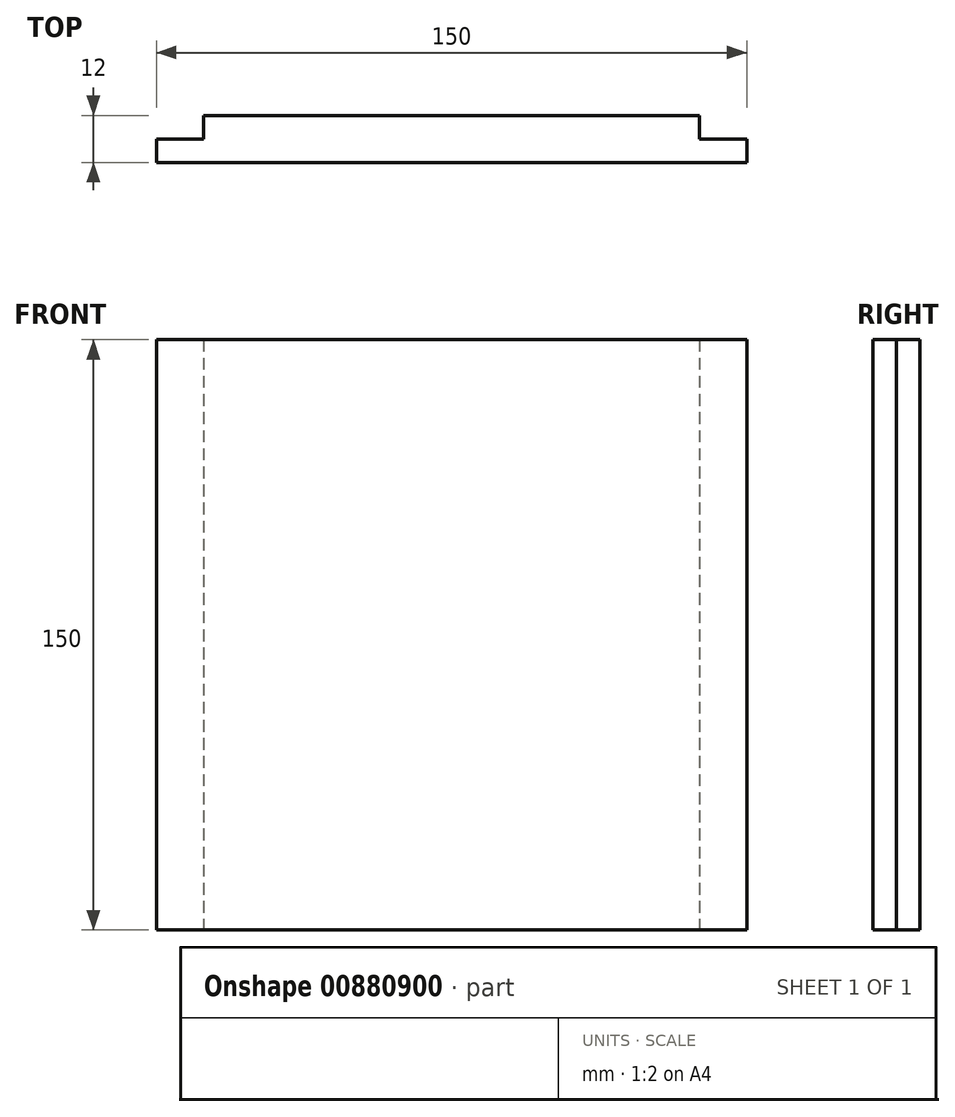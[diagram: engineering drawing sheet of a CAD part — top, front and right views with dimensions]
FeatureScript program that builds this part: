
annotation { "Feature Type Name" : "Feature", "Feature Type Description" : "" }
export const myFeature = defineFeature(function(context is Context, id is Id, definition is map)
    precondition{}
    {
        {
            var Q0;
            Q0=qCreatedBy(makeId("Top.planeOp"),FACE);
            var sketch = newSketch(context, id + "F0", { "sketchPlane" : qUnion([Q0])});
            skLineSegment(sketch, "E0.bottom", {"start": v(63, 6) * mm, "end": v(-63, 6) * mm});
            skLineSegment(sketch, "E0.top", {"start": v(75, -6) * mm, "end": v(-75, -6) * mm});
            skLineSegment(sketch, "E0.left", {"start": v(75, 0) * mm, "end": v(75, -6) * mm});
            skLineSegment(sketch, "E0.right", {"start": v(-75, 0) * mm, "end": v(-75, -6) * mm});
            skPoint(sketch, "E0.middle", {"position": v(0, 0) * mm});
            skLineSegment(sketch, "E1", {"start": v(-75, 0) * mm, "end": v(-63, 0) * mm});
            skLineSegment(sketch, "E2", {"start": v(-63, 0) * mm, "end": v(-63, 6) * mm});
            skLineSegment(sketch, "E3", {"start": v(75, 0) * mm, "end": v(63, 0) * mm});
            skLineSegment(sketch, "E4", {"start": v(63, 0) * mm, "end": v(63, 6) * mm});
            skPoint(sketch, "E5.orphan", {"position": v(75, 6) * mm});
            skPoint(sketch, "E6.orphan", {"position": v(-75, 6) * mm});
            skSolve(sketch);
        }
        {
            var Q0;
            Q0=makeQuery(id+"F0.imprint","IMPRINT",FACE,{"disambiguationData":[TD([[makeQuery(id+"F0.imprint","IMPRINT",EDGE,{"derivedFrom":sQuery(id+"F0.wireOp",EDGE,"E0.bottom")}),1.0]])]});
            extrude(context, id + "F1", {"entities" : qUnion([Q0]), "depth" : 150 * mm, "offsetDistance" : 25 * mm});
        }
    });
